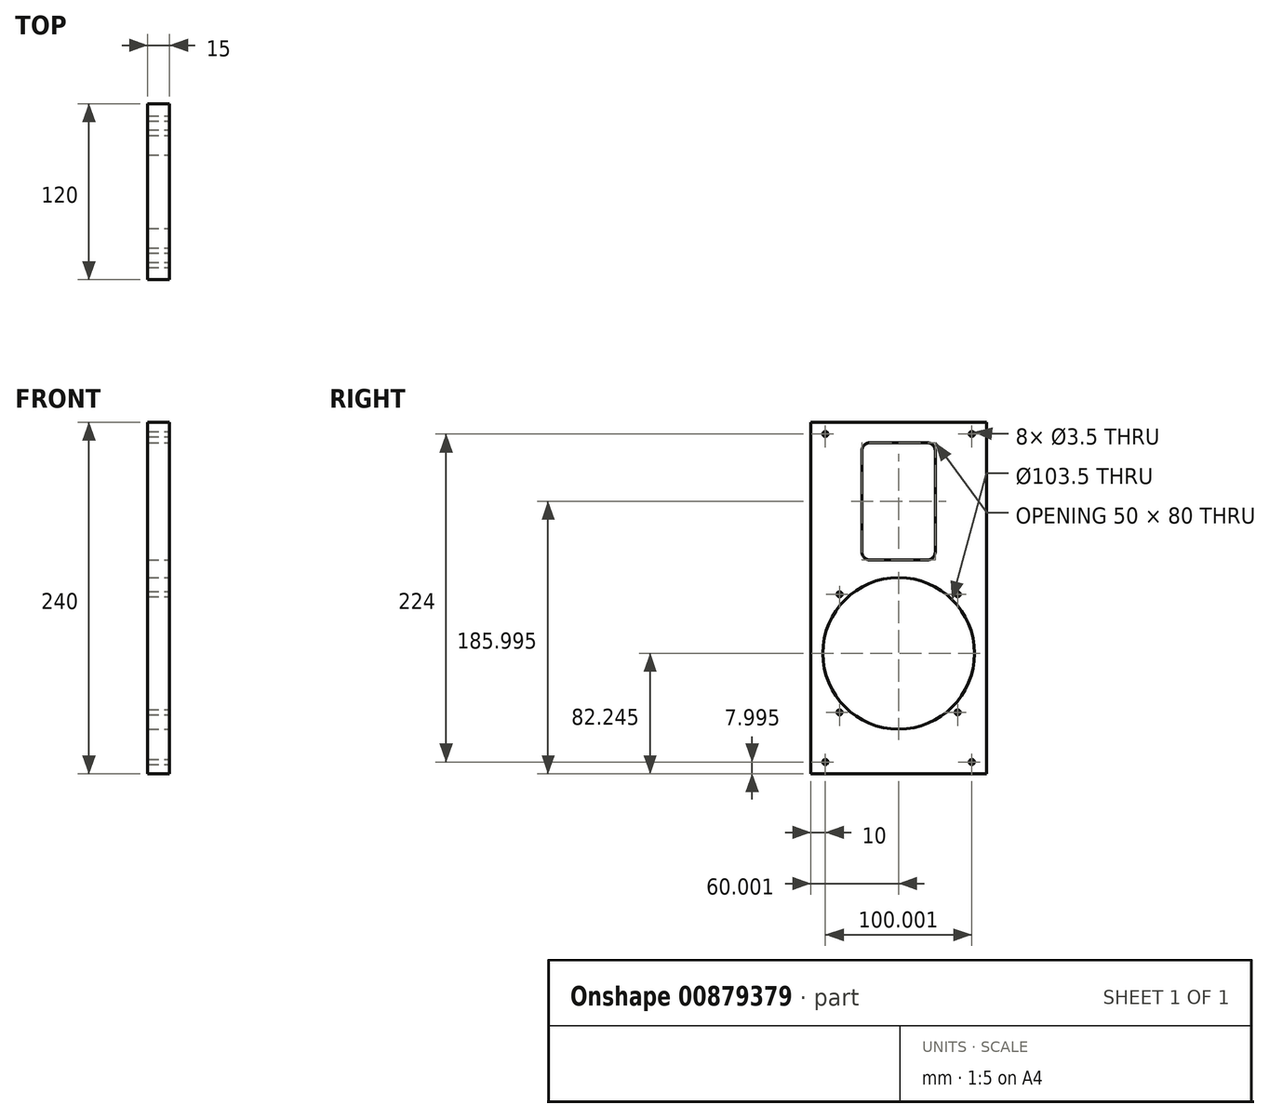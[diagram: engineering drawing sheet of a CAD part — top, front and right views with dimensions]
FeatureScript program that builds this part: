
annotation { "Feature Type Name" : "Feature", "Feature Type Description" : "" }
export const myFeature = defineFeature(function(context is Context, id is Id, definition is map)
    precondition{}
    {
        {
            var Q0;
            Q0=qCreatedBy(makeId("Right.planeOp"),FACE);
            var sketch = newSketch(context, id + "F0", { "sketchPlane" : qUnion([Q0])});
            skLineSegment(sketch, "E0", {"start": v(60, -115.06) * mm, "end": v(-60, -115.06) * mm});
            skPoint(sketch, "E1", {"position": v(0, -32.81) * mm});
            skCircle(sketch, "E2", {"center": v(0, -32.81) * mm, "radius": 51.75 * mm});
            skCircle(sketch, "E3", {"center": v(40.3, 7.5) * mm, "radius": 1.75 * mm});
            skCircle(sketch, "E4.1.0", {"center": v(-40.3, 7.5) * mm, "radius": 1.75 * mm});
            skCircle(sketch, "E4.2.0", {"center": v(-40.3, -73.12) * mm, "radius": 1.75 * mm});
            skCircle(sketch, "E4.3.0", {"center": v(40.3, -73.12) * mm, "radius": 1.75 * mm});
            skPoint(sketch, "E5", {"position": v(-193.88, 39.27) * mm});
            skLineSegment(sketch, "E6", {"start": v(-60, 124.94) * mm, "end": v(-60, -115.06) * mm});
            skLineSegment(sketch, "E7.trimOffspring", {"start": v(0, 70.84) * mm, "end": v(0, 70.94) * mm});
            skLineSegment(sketch, "E8.bottom", {"start": v(12, 103.45) * mm, "end": v(-12, 103.45) * mm});
            skLineSegment(sketch, "E8.left", {"start": v(15, 100.45) * mm, "end": v(15, 38.42) * mm});
            skLineSegment(sketch, "E8.right", {"start": v(-15, 100.45) * mm, "end": v(-15, 38.42) * mm});
            skPoint(sketch, "E8.middle", {"position": v(0, 70.94) * mm});
            skCircle(sketch, "E9", {"center": v(19, 104.94) * mm, "radius": 2 * mm});
            skCircle(sketch, "E10.0.1.0", {"center": v(19, 36.94) * mm, "radius": 2 * mm});
            skCircle(sketch, "E10.1.0.0", {"center": v(-19, 104.94) * mm, "radius": 2 * mm});
            skCircle(sketch, "E10.1.1.0", {"center": v(-19, 36.94) * mm, "radius": 2 * mm});
            skLineSegment(sketch, "E10.direction1", {"start": v(19, 104.94) * mm, "end": v(17, 104.94) * mm, "construction": true});
            skLineSegment(sketch, "E10.direction2", {"start": v(19, 104.94) * mm, "end": v(19, 102.94) * mm, "construction": true});
            skLineSegment(sketch, "E11", {"start": v(19.5, 110.94) * mm, "end": v(-19.5, 110.94) * mm});
            skLineSegment(sketch, "E12", {"start": v(-25, 105.44) * mm, "end": v(-25, 36.44) * mm});
            skLineSegment(sketch, "E13", {"start": v(-19.5, 30.94) * mm, "end": v(19.5, 30.94) * mm});
            skLineSegment(sketch, "E14", {"start": v(25, 105.44) * mm, "end": v(25, 36.44) * mm});
            skPoint(sketch, "E15.visualSharp", {"position": v(25, 110.94) * mm});
            skArc(sketch, "E15.filletArc", {"start": v(25, 105.44) * mm, "mid": v(23.39, 109.32) * mm, "end": v(19.5, 110.94) * mm});
            skPoint(sketch, "E16.visualSharp", {"position": v(-25, 110.94) * mm});
            skArc(sketch, "E16.filletArc", {"start": v(-19.5, 110.94) * mm, "mid": v(-23.39, 109.32) * mm, "end": v(-25, 105.44) * mm});
            skPoint(sketch, "E17.visualSharp", {"position": v(-25, 30.94) * mm});
            skArc(sketch, "E17.filletArc", {"start": v(-25, 36.44) * mm, "mid": v(-23.39, 32.55) * mm, "end": v(-19.5, 30.94) * mm});
            skPoint(sketch, "E18.visualSharp", {"position": v(25, 30.94) * mm});
            skArc(sketch, "E18.filletArc", {"start": v(19.5, 30.94) * mm, "mid": v(23.39, 32.55) * mm, "end": v(25, 36.44) * mm});
            skLineSegment(sketch, "E19.trimOffspring", {"start": v(0, 70.94) * mm, "end": v(0, 70.84) * mm});
            skPoint(sketch, "E20.visualSharp", {"position": v(15, 103.45) * mm});
            skArc(sketch, "E20.filletArc", {"start": v(15, 100.45) * mm, "mid": v(14.12, 102.57) * mm, "end": v(12, 103.45) * mm});
            skPoint(sketch, "E21.visualSharp", {"position": v(-15, 103.45) * mm});
            skArc(sketch, "E21.filletArc", {"start": v(-12, 103.45) * mm, "mid": v(-14.12, 102.57) * mm, "end": v(-15, 100.45) * mm});
            skLineSegment(sketch, "E22.top", {"start": v(12, 33.8) * mm, "end": v(-12, 33.8) * mm});
            skLineSegment(sketch, "E22.left", {"start": v(15, 38.42) * mm, "end": v(15, 36.8) * mm});
            skLineSegment(sketch, "E22.right", {"start": v(-15, 38.42) * mm, "end": v(-15, 36.8) * mm});
            skPoint(sketch, "E23.visualSharp", {"position": v(15, 33.8) * mm});
            skArc(sketch, "E23.filletArc", {"start": v(12, 33.8) * mm, "mid": v(14.12, 34.67) * mm, "end": v(15, 36.8) * mm});
            skPoint(sketch, "E24.visualSharp", {"position": v(-15, 33.8) * mm});
            skArc(sketch, "E24.filletArc", {"start": v(-15, 36.8) * mm, "mid": v(-14.12, 34.67) * mm, "end": v(-12, 33.8) * mm});
            skLineSegment(sketch, "E25.top", {"start": v(-60, -115.06) * mm, "end": v(60, -115.06) * mm});
            skLineSegment(sketch, "E26", {"start": v(60, 124.94) * mm, "end": v(60, -115.06) * mm});
            skLineSegment(sketch, "E27.bottom", {"start": v(-60, 124.94) * mm, "end": v(0, 124.94) * mm});
            skPoint(sketch, "E28.trimOffspring.end.orphan", {"position": v(0, -115.06) * mm});
            skCircle(sketch, "E29.0.1.0", {"center": v(-50, 116.94) * mm, "radius": 1.75 * mm});
            skCircle(sketch, "E30.0.1.0", {"center": v(50, 116.94) * mm, "radius": 1.75 * mm});
            skCircle(sketch, "E31.0.1.0", {"center": v(50, -107.06) * mm, "radius": 1.75 * mm});
            skCircle(sketch, "E32.0.1.0", {"center": v(-50, -107.06) * mm, "radius": 1.75 * mm});
            skLineSegment(sketch, "E33.trimOffspring", {"start": v(-17, 104.94) * mm, "end": v(-19, 104.94) * mm, "construction": true});
            skLineSegment(sketch, "E34.trimOffspring", {"start": v(19, 38.94) * mm, "end": v(19, 36.94) * mm, "construction": true});
            skLineSegment(sketch, "E35", {"start": v(60, 124.94) * mm, "end": v(0, 124.94) * mm});
            skSolve(sketch);
        }
        {
            var Q0;
            Q0=makeQuery(id+"F0.imprint","IMPRINT",FACE,{"disambiguationData":[TD([[makeQuery(id+"F0.imprint","IMPRINT",EDGE,{"derivedFrom":sQuery(id+"F0.wireOp",EDGE,"E2")}),-1.0]])]});
            extrude(context, id + "F1", {"entities" : qUnion([Q0]), "oppositeDirection" : true, "depth" : 15 * mm, "offsetDistance" : 25 * mm});
        }
    });
